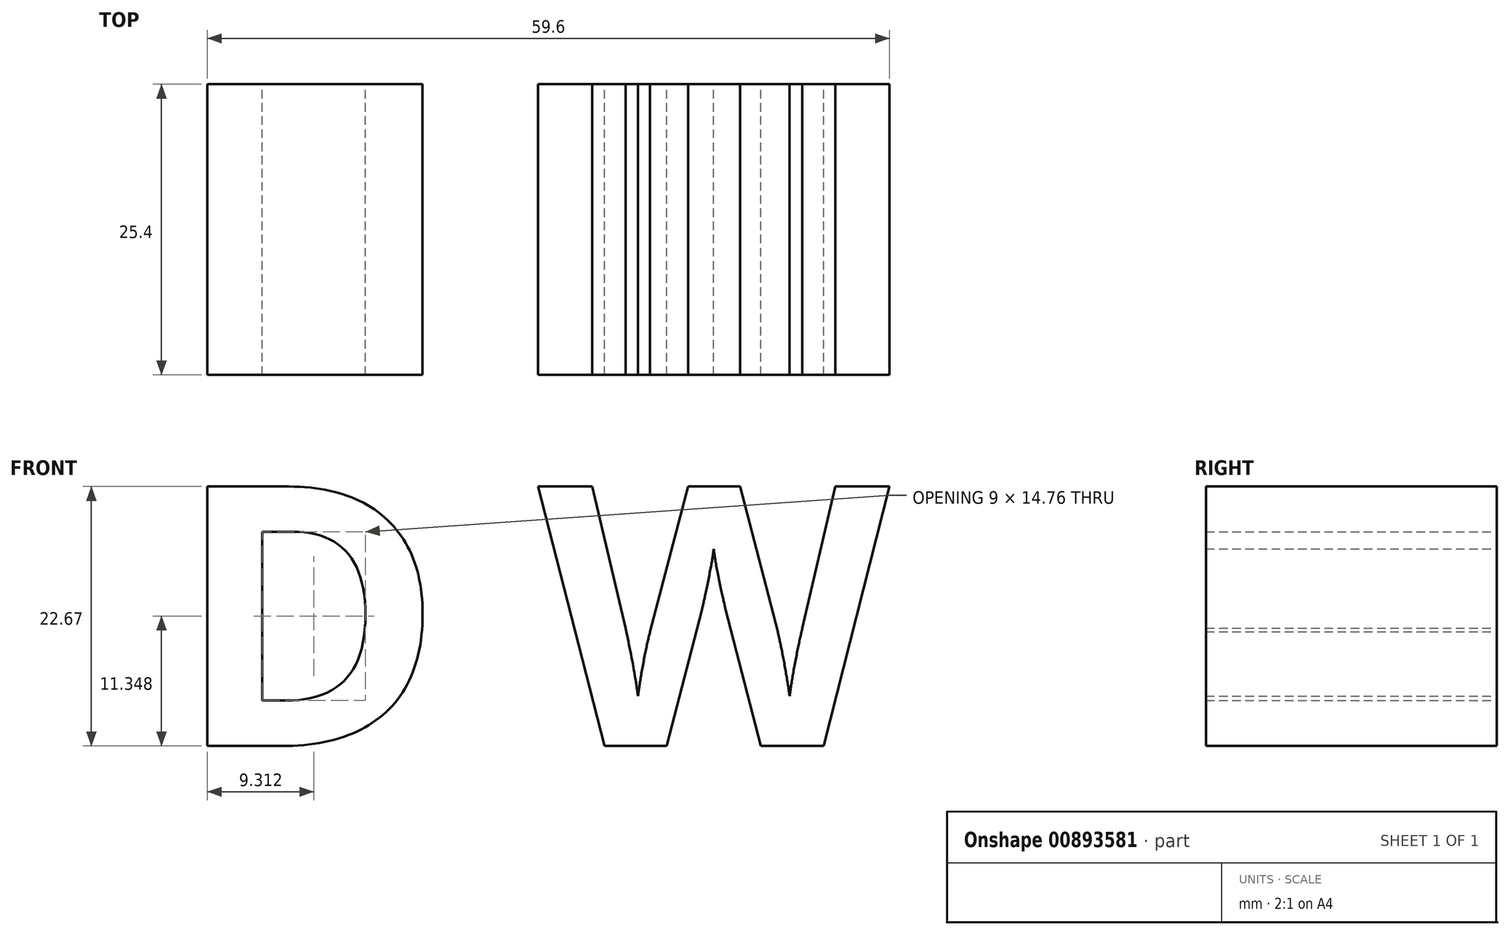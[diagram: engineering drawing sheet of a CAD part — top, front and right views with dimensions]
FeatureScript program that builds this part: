
annotation { "Feature Type Name" : "Feature", "Feature Type Description" : "" }
export const myFeature = defineFeature(function(context is Context, id is Id, definition is map)
    precondition{}
    {
        {
            var Q0;
            Q0=qCreatedBy(makeId("Front.planeOp"),FACE);
            var sketch = newSketch(context, id + "F0", { "sketchPlane" : qUnion([Q0])});
            skText(sketch, "E0", { "text": "D W", "fontName": "OpenSans-Bold.ttf"});
            const initialGuessF0  = {"E0": [-0.02425, 0, 1, 0, 0.02286]};
            skSetInitialGuess(sketch, initialGuessF0);
            skSolve(sketch);
        }
        {
            var Q0;
            Q0 = qSketchRegion(id + "F0", true);
            extrude(context, id + "F1", {"entities" : qUnion([Q0]), "depth" : 25.4 * mm, "offsetDistance" : 25.4 * mm});
        }
    });
